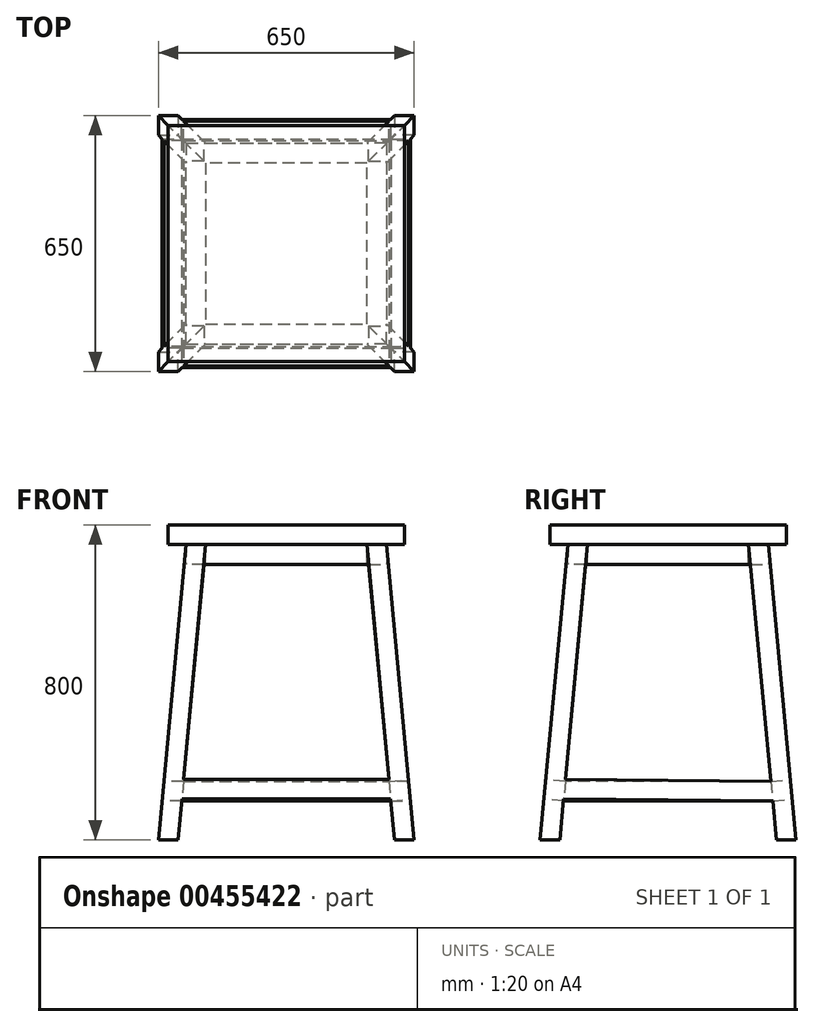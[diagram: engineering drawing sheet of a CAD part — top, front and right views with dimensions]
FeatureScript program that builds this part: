
annotation { "Feature Type Name" : "Feature", "Feature Type Description" : "" }
export const myFeature = defineFeature(function(context is Context, id is Id, definition is map)
    precondition{}
    {
        {
            var Q0;
            Q0=qCreatedBy(makeId("Top.planeOp"),FACE);
            var sketch = newSketch(context, id + "F0", { "sketchPlane" : qUnion([Q0])});
            skLineSegment(sketch, "E0.bottom", {"start": v(-250, 250) * mm, "end": v(250, 250) * mm, "construction": true});
            skLineSegment(sketch, "E0.top", {"start": v(-250, -250) * mm, "end": v(250, -250) * mm, "construction": true});
            skLineSegment(sketch, "E0.left", {"start": v(-250, 250) * mm, "end": v(-250, -250) * mm, "construction": true});
            skLineSegment(sketch, "E0.right", {"start": v(250, 250) * mm, "end": v(250, -250) * mm, "construction": true});
            skPoint(sketch, "E0.middle", {"position": v(0, 0) * mm});
            skLineSegment(sketch, "E1.bottom", {"start": v(-250, -250) * mm, "end": v(-200, -250) * mm});
            skLineSegment(sketch, "E1.top", {"start": v(-250, -200) * mm, "end": v(-200, -200) * mm});
            skLineSegment(sketch, "E1.left", {"start": v(-250, -250) * mm, "end": v(-250, -200) * mm});
            skLineSegment(sketch, "E1.right", {"start": v(-200, -250) * mm, "end": v(-200, -200) * mm});
            skLineSegment(sketch, "E2.bottom", {"start": v(250, -250) * mm, "end": v(200, -250) * mm});
            skLineSegment(sketch, "E2.top", {"start": v(250, -200) * mm, "end": v(200, -200) * mm});
            skLineSegment(sketch, "E2.left", {"start": v(250, -250) * mm, "end": v(250, -200) * mm});
            skLineSegment(sketch, "E2.right", {"start": v(200, -250) * mm, "end": v(200, -200) * mm});
            skLineSegment(sketch, "E3.bottom", {"start": v(250, 250) * mm, "end": v(200, 250) * mm});
            skLineSegment(sketch, "E3.top", {"start": v(250, 200) * mm, "end": v(200, 200) * mm});
            skLineSegment(sketch, "E3.left", {"start": v(250, 250) * mm, "end": v(250, 200) * mm});
            skLineSegment(sketch, "E3.right", {"start": v(200, 250) * mm, "end": v(200, 200) * mm});
            skLineSegment(sketch, "E4.bottom", {"start": v(-250, 250) * mm, "end": v(-200, 250) * mm});
            skLineSegment(sketch, "E4.top", {"start": v(-250, 200) * mm, "end": v(-200, 200) * mm});
            skLineSegment(sketch, "E4.left", {"start": v(-250, 250) * mm, "end": v(-250, 200) * mm});
            skLineSegment(sketch, "E4.right", {"start": v(-200, 250) * mm, "end": v(-200, 200) * mm});
            skSolve(sketch);
        }
        {
            var Q0;
            Q0=qCreatedBy(makeId("Top.planeOp"),FACE);
            cPlane(context, id + "F1", {"entities" : qUnion([Q0]), "cplaneType" : CPlaneType.OFFSET, "offset" : 800 * mm, "oppositeDirection" : true, "width" : 150 * mm, "height" : 150 * mm});
        }
        {
            var Q0;
            Q0=qCreatedBy(id+"F1.planeOp",FACE);
            var sketch = newSketch(context, id + "F2", { "sketchPlane" : qUnion([Q0])});
            skLineSegment(sketch, "E5.bottom", {"start": v(-325, 325) * mm, "end": v(325, 325) * mm, "construction": true});
            skLineSegment(sketch, "E5.top", {"start": v(-325, -325) * mm, "end": v(325, -325) * mm, "construction": true});
            skLineSegment(sketch, "E5.left", {"start": v(-325, 325) * mm, "end": v(-325, -325) * mm, "construction": true});
            skLineSegment(sketch, "E5.right", {"start": v(325, 325) * mm, "end": v(325, -325) * mm, "construction": true});
            skPoint(sketch, "E5.middle", {"position": v(0, 0) * mm});
            skLineSegment(sketch, "E6.bottom", {"start": v(-325, -325) * mm, "end": v(-275, -325) * mm});
            skLineSegment(sketch, "E6.top", {"start": v(-325, -275) * mm, "end": v(-275, -275) * mm});
            skLineSegment(sketch, "E6.left", {"start": v(-325, -325) * mm, "end": v(-325, -275) * mm});
            skLineSegment(sketch, "E6.right", {"start": v(-275, -325) * mm, "end": v(-275, -275) * mm});
            skLineSegment(sketch, "E7.bottom", {"start": v(325, -325) * mm, "end": v(275, -325) * mm});
            skLineSegment(sketch, "E7.top", {"start": v(325, -275) * mm, "end": v(275, -275) * mm});
            skLineSegment(sketch, "E7.left", {"start": v(325, -325) * mm, "end": v(325, -275) * mm});
            skLineSegment(sketch, "E7.right", {"start": v(275, -325) * mm, "end": v(275, -275) * mm});
            skLineSegment(sketch, "E8.bottom", {"start": v(325, 325) * mm, "end": v(275, 325) * mm});
            skLineSegment(sketch, "E8.top", {"start": v(325, 275) * mm, "end": v(275, 275) * mm});
            skLineSegment(sketch, "E8.left", {"start": v(325, 325) * mm, "end": v(325, 275) * mm});
            skLineSegment(sketch, "E8.right", {"start": v(275, 325) * mm, "end": v(275, 275) * mm});
            skLineSegment(sketch, "E9.bottom", {"start": v(-325, 325) * mm, "end": v(-275, 325) * mm});
            skLineSegment(sketch, "E9.top", {"start": v(-325, 275) * mm, "end": v(-275, 275) * mm});
            skLineSegment(sketch, "E9.left", {"start": v(-325, 325) * mm, "end": v(-325, 275) * mm});
            skLineSegment(sketch, "E9.right", {"start": v(-275, 325) * mm, "end": v(-275, 275) * mm});
            skSolve(sketch);
        }
        {
            var Q0;
            Q0=qCreatedBy(makeId("Top.planeOp"),FACE);
            var sketch = newSketch(context, id + "F3", { "sketchPlane" : qUnion([Q0])});
            skLineSegment(sketch, "E10.bottom", {"start": v(-300, 300) * mm, "end": v(300, 300) * mm});
            skLineSegment(sketch, "E10.top", {"start": v(-300, -300) * mm, "end": v(300, -300) * mm});
            skLineSegment(sketch, "E10.left", {"start": v(-300, 300) * mm, "end": v(-300, -300) * mm});
            skLineSegment(sketch, "E10.right", {"start": v(300, 300) * mm, "end": v(300, -300) * mm});
            skPoint(sketch, "E10.middle", {"position": v(0, 0) * mm});
            skSolve(sketch);
        }
        {
            var Q0;
            Q0=makeQuery(id+"F0.imprint","IMPRINT",FACE,{"disambiguationData":[TD([[makeQuery(id+"F0.imprint","IMPRINT",EDGE,{"derivedFrom":sQuery(id+"F0.wireOp",EDGE,"E1.bottom")}),1.0]])]});
            var Q1;
            Q1=makeQuery(id+"F2.imprint","IMPRINT",FACE,{"disambiguationData":[TD([[makeQuery(id+"F2.imprint","IMPRINT",EDGE,{"derivedFrom":sQuery(id+"F2.wireOp",EDGE,"E6.bottom")}),1.0]])]});
            loft(context, id + "F4", {"sheetProfilesArray" : [{ "sheetProfileEntities" : qUnion([Q0]) }, { "sheetProfileEntities" : qUnion([Q1]) }]});
        }
        {
            var Q0;
            Q0=makeQuery(id+"F0.imprint","IMPRINT",FACE,{"disambiguationData":[TD([[makeQuery(id+"F0.imprint","IMPRINT",EDGE,{"derivedFrom":sQuery(id+"F0.wireOp",EDGE,"E2.bottom")}),-1.0]])]});
            var Q1;
            Q1=makeQuery(id+"F2.imprint","IMPRINT",FACE,{"disambiguationData":[TD([[makeQuery(id+"F2.imprint","IMPRINT",EDGE,{"derivedFrom":sQuery(id+"F2.wireOp",EDGE,"E7.bottom")}),-1.0]])]});
            loft(context, id + "F5", {"sheetProfilesArray" : [{ "sheetProfileEntities" : qUnion([Q0]) }, { "sheetProfileEntities" : qUnion([Q1]) }]});
        }
        {
            var Q0;
            Q0=makeQuery(id+"F0.imprint","IMPRINT",FACE,{"disambiguationData":[TD([[makeQuery(id+"F0.imprint","IMPRINT",EDGE,{"derivedFrom":sQuery(id+"F0.wireOp",EDGE,"E4.bottom")}),-1.0]])]});
            var Q1;
            Q1=makeQuery(id+"F2.imprint","IMPRINT",FACE,{"disambiguationData":[TD([[makeQuery(id+"F2.imprint","IMPRINT",EDGE,{"derivedFrom":sQuery(id+"F2.wireOp",EDGE,"E9.bottom")}),-1.0]])]});
            loft(context, id + "F6", {"sheetProfilesArray" : [{ "sheetProfileEntities" : qUnion([Q0]) }, { "sheetProfileEntities" : qUnion([Q1]) }]});
        }
        {
            var Q0;
            Q0=makeQuery(id+"F0.imprint","IMPRINT",FACE,{"disambiguationData":[TD([[makeQuery(id+"F0.imprint","IMPRINT",EDGE,{"derivedFrom":sQuery(id+"F0.wireOp",EDGE,"E3.bottom")}),1.0]])]});
            var Q1;
            Q1=makeQuery(id+"F2.imprint","IMPRINT",FACE,{"disambiguationData":[TD([[makeQuery(id+"F2.imprint","IMPRINT",EDGE,{"derivedFrom":sQuery(id+"F2.wireOp",EDGE,"E8.bottom")}),1.0]])]});
            loft(context, id + "F7", {"sheetProfilesArray" : [{ "sheetProfileEntities" : qUnion([Q0]) }, { "sheetProfileEntities" : qUnion([Q1]) }]});
        }
        {
            var Q0;
            Q0 = qSketchRegion(id + "F3", true);
            extrude(context, id + "F8", {"entities" : qUnion([Q0]), "operationType" : NewBodyOperationType.ADD, "oppositeDirection" : true, "depth" : 50 * mm});
        }
        {
            var Q0;
            Q0=makeQuery(id+"F8.opExtrude","CAP_FACE",FACE,{"disambiguationData":[OSD([sQuery(id+"F3.wireOp",EDGE,"E10.bottom"),sQuery(id+"F3.wireOp",EDGE,"E10.top"),sQuery(id+"F3.wireOp",EDGE,"E10.left"),sQuery(id+"F3.wireOp",EDGE,"E10.right")])],"isStart":false});
            var sketch = newSketch(context, id + "F9", { "sketchPlane" : qUnion([Q0])});
            skLineSegment(sketch, "E11", {"start": v(204.69, 204.69) * mm, "end": v(204.69, -204.69) * mm});
            skLineSegment(sketch, "E12", {"start": v(254.69, -204.69) * mm, "end": v(254.69, 204.69) * mm});
            skLineSegment(sketch, "E13", {"start": v(-204.69, -204.69) * mm, "end": v(-204.69, 204.69) * mm});
            skLineSegment(sketch, "E14", {"start": v(-204.69, 204.69) * mm, "end": v(204.69, 204.69) * mm});
            skLineSegment(sketch, "E15", {"start": v(204.69, 254.69) * mm, "end": v(-204.69, 254.69) * mm});
            skLineSegment(sketch, "E16", {"start": v(204.69, -254.69) * mm, "end": v(-204.69, -254.69) * mm});
            skLineSegment(sketch, "E17", {"start": v(-204.69, 254.69) * mm, "end": v(-254.69, 254.69) * mm});
            skLineSegment(sketch, "E18", {"start": v(-254.69, 254.69) * mm, "end": v(-254.69, -254.69) * mm});
            skLineSegment(sketch, "E19", {"start": v(-254.69, -254.69) * mm, "end": v(-204.69, -254.69) * mm});
            skLineSegment(sketch, "E20", {"start": v(204.69, -254.69) * mm, "end": v(254.69, -254.69) * mm});
            skLineSegment(sketch, "E21", {"start": v(254.69, -254.69) * mm, "end": v(254.69, -204.69) * mm});
            skLineSegment(sketch, "E22", {"start": v(254.69, 204.69) * mm, "end": v(254.69, 254.69) * mm});
            skLineSegment(sketch, "E23", {"start": v(254.69, 254.69) * mm, "end": v(204.69, 254.69) * mm});
            skLineSegment(sketch, "E24", {"start": v(204.69, -204.69) * mm, "end": v(-204.69, -204.69) * mm});
            skSolve(sketch);
        }
        {
            var Q0;
            Q0 = qSketchRegion(id + "F9", true);
            extrude(context, id + "F10", {"entities" : qUnion([Q0]), "operationType" : NewBodyOperationType.ADD, "depth" : 50 * mm});
        }
        {
            var Q0;
            Q0=qCreatedBy(id+"F1.planeOp",FACE);
            cPlane(context, id + "F11", {"entities" : qUnion([Q0]), "cplaneType" : CPlaneType.OFFSET, "offset" : 80 * mm, "width" : 150 * mm, "height" : 150 * mm});
        }
        {
            var Q0;
            Q0=makeQuery(id+"F6.opLoft","SWEPT_FACE",FACE,{"disambiguationData":[OSD([sQuery(id+"F0.wireOp",EDGE,"E4.top"),sQuery(id+"F0.wireOp",EDGE,"E4.left"),sQuery(id+"F0.wireOp",EDGE,"E4.right"),sQuery(id+"F2.wireOp",EDGE,"E9.top"),sQuery(id+"F2.wireOp",EDGE,"E9.left"),sQuery(id+"F2.wireOp",EDGE,"E9.right")])]});
            var sketch = newSketch(context, id + "F12", { "sketchPlane" : qUnion([Q0])});
            skLineSegment(sketch, "E25", {"start": v(-275, -822.18) * mm, "end": v(-265.7, -722.6) * mm, "construction": true});
            skLineSegment(sketch, "E26", {"start": v(-265.7, -722.6) * mm, "end": v(-261.06, -672.83) * mm});
            skLineSegment(sketch, "E27", {"start": v(-311.06, -672.83) * mm, "end": v(-315.7, -722.6) * mm});
            skLineSegment(sketch, "E28", {"start": v(-315.7, -722.6) * mm, "end": v(-265.7, -722.6) * mm});
            skLineSegment(sketch, "E29", {"start": v(-261.06, -672.83) * mm, "end": v(-311.06, -672.83) * mm});
            skSolve(sketch);
        }
        {
            var Q0;
            Q0=makeQuery(id+"F6.opLoft","SWEPT_FACE",FACE,{"disambiguationData":[OSD([sQuery(id+"F0.wireOp",EDGE,"E4.bottom"),sQuery(id+"F0.wireOp",EDGE,"E4.top"),sQuery(id+"F0.wireOp",EDGE,"E4.right"),sQuery(id+"F2.wireOp",EDGE,"E9.bottom"),sQuery(id+"F2.wireOp",EDGE,"E9.top"),sQuery(id+"F2.wireOp",EDGE,"E9.right")])]});
            var sketch = newSketch(context, id + "F13", { "sketchPlane" : qUnion([Q0])});
            skLineSegment(sketch, "E30", {"start": v(275, -822.18) * mm, "end": v(265.7, -722.6) * mm, "construction": true});
            skLineSegment(sketch, "E31", {"start": v(265.7, -722.6) * mm, "end": v(261.06, -672.83) * mm});
            skLineSegment(sketch, "E32", {"start": v(265.7, -722.6) * mm, "end": v(315.27, -717.98) * mm});
            skLineSegment(sketch, "E33", {"start": v(261.06, -672.83) * mm, "end": v(310.63, -668.2) * mm});
            skLineSegment(sketch, "E34", {"start": v(310.63, -668.2) * mm, "end": v(315.27, -717.98) * mm});
            skSolve(sketch);
        }
        {
            var Q0;
            Q0=makeQuery(id+"F7.opLoft","SWEPT_FACE",FACE,{"disambiguationData":[OSD([sQuery(id+"F0.wireOp",EDGE,"E3.bottom"),sQuery(id+"F0.wireOp",EDGE,"E3.top"),sQuery(id+"F0.wireOp",EDGE,"E3.right"),sQuery(id+"F2.wireOp",EDGE,"E8.bottom"),sQuery(id+"F2.wireOp",EDGE,"E8.top"),sQuery(id+"F2.wireOp",EDGE,"E8.right")])]});
            var sketch = newSketch(context, id + "F14", { "sketchPlane" : qUnion([Q0])});
            skLineSegment(sketch, "E35", {"start": v(-275, -822.18) * mm, "end": v(-265.7, -722.6) * mm, "construction": true});
            skLineSegment(sketch, "E36", {"start": v(-265.7, -722.6) * mm, "end": v(-261.06, -672.83) * mm});
            skLineSegment(sketch, "E37", {"start": v(-261.06, -672.83) * mm, "end": v(-310.63, -668.2) * mm});
            skLineSegment(sketch, "E38", {"start": v(-265.7, -722.6) * mm, "end": v(-315.27, -717.98) * mm});
            skLineSegment(sketch, "E39", {"start": v(-315.27, -717.98) * mm, "end": v(-310.63, -668.2) * mm});
            skSolve(sketch);
        }
        {
            var Q1;
            Q1=makeQuery(id+"F13.imprint","IMPRINT",FACE,{"disambiguationData":[TD([[makeQuery(id+"F13.imprint","IMPRINT",EDGE,{"derivedFrom":sQuery(id+"F13.wireOp",EDGE,"E31")}),1.0]])]});
            var Q2;
            Q2=makeQuery(id+"F14.imprint","IMPRINT",FACE,{"disambiguationData":[TD([[makeQuery(id+"F14.imprint","IMPRINT",EDGE,{"derivedFrom":sQuery(id+"F14.wireOp",EDGE,"E36")}),-1.0]])]});
            loft(context, id + "F15", {"operationType" : NewBodyOperationType.ADD, "sheetProfilesArray" : [{ "sheetProfileEntities" : qUnion([Q1]) }, { "sheetProfileEntities" : qUnion([Q2]) }]});
        }
        {
            var Q0;
            Q0=makeQuery(id+"F4.opLoft","SWEPT_FACE",FACE,{"disambiguationData":[OSD([sQuery(id+"F0.wireOp",EDGE,"E1.top"),sQuery(id+"F0.wireOp",EDGE,"E1.left"),sQuery(id+"F0.wireOp",EDGE,"E1.right"),sQuery(id+"F2.wireOp",EDGE,"E6.top"),sQuery(id+"F2.wireOp",EDGE,"E6.left"),sQuery(id+"F2.wireOp",EDGE,"E6.right")])]});
            var sketch = newSketch(context, id + "F16", { "sketchPlane" : qUnion([Q0])});
            skLineSegment(sketch, "E40", {"start": v(275, -822.18) * mm, "end": v(265.7, -722.6) * mm, "construction": true});
            skLineSegment(sketch, "E41", {"start": v(265.7, -722.6) * mm, "end": v(315.7, -722.6) * mm});
            skLineSegment(sketch, "E42", {"start": v(265.7, -722.6) * mm, "end": v(261.06, -672.83) * mm});
            skLineSegment(sketch, "E43", {"start": v(261.06, -672.83) * mm, "end": v(311.06, -672.83) * mm});
            skLineSegment(sketch, "E44", {"start": v(311.06, -672.83) * mm, "end": v(315.7, -722.6) * mm});
            skSolve(sketch);
        }
        {
            var Q0;
            Q0=makeQuery(id+"F4.opLoft","SWEPT_FACE",FACE,{"disambiguationData":[OSD([sQuery(id+"F0.wireOp",EDGE,"E1.bottom"),sQuery(id+"F0.wireOp",EDGE,"E1.top"),sQuery(id+"F0.wireOp",EDGE,"E1.right"),sQuery(id+"F2.wireOp",EDGE,"E6.bottom"),sQuery(id+"F2.wireOp",EDGE,"E6.top"),sQuery(id+"F2.wireOp",EDGE,"E6.right")])]});
            var sketch = newSketch(context, id + "F17", { "sketchPlane" : qUnion([Q0])});
            skLineSegment(sketch, "E45", {"start": v(-275, -822.18) * mm, "end": v(-265.7, -722.6) * mm, "construction": true});
            skLineSegment(sketch, "E46", {"start": v(-265.7, -722.6) * mm, "end": v(-261.06, -672.83) * mm});
            skLineSegment(sketch, "E47", {"start": v(-265.7, -722.6) * mm, "end": v(-315.27, -717.98) * mm});
            skLineSegment(sketch, "E48", {"start": v(-261.06, -672.83) * mm, "end": v(-310.63, -668.2) * mm});
            skLineSegment(sketch, "E49", {"start": v(-310.63, -668.2) * mm, "end": v(-315.27, -717.98) * mm});
            skSolve(sketch);
        }
        {
            var Q1;
            Q1=makeQuery(id+"F12.imprint","IMPRINT",FACE,{"disambiguationData":[TD([[makeQuery(id+"F12.imprint","IMPRINT",EDGE,{"derivedFrom":sQuery(id+"F12.wireOp",EDGE,"E26")}),-1.0]])]});
            var Q2;
            Q2=makeQuery(id+"F16.imprint","IMPRINT",FACE,{"disambiguationData":[TD([[makeQuery(id+"F16.imprint","IMPRINT",EDGE,{"derivedFrom":sQuery(id+"F16.wireOp",EDGE,"E41")}),1.0]])]});
            loft(context, id + "F18", {"operationType" : NewBodyOperationType.ADD, "sheetProfilesArray" : [{ "sheetProfileEntities" : qUnion([Q1]) }, { "sheetProfileEntities" : qUnion([Q2]) }]});
        }
        {
            var Q0;
            Q0=makeQuery(id+"F5.opLoft","SWEPT_FACE",FACE,{"disambiguationData":[OSD([sQuery(id+"F0.wireOp",EDGE,"E2.bottom"),sQuery(id+"F0.wireOp",EDGE,"E2.top"),sQuery(id+"F0.wireOp",EDGE,"E2.right"),sQuery(id+"F2.wireOp",EDGE,"E7.bottom"),sQuery(id+"F2.wireOp",EDGE,"E7.top"),sQuery(id+"F2.wireOp",EDGE,"E7.right")])]});
            var sketch = newSketch(context, id + "F19", { "sketchPlane" : qUnion([Q0])});
            skLineSegment(sketch, "E50", {"start": v(275, -822.18) * mm, "end": v(265.7, -722.6) * mm, "construction": true});
            skLineSegment(sketch, "E51", {"start": v(265.7, -722.6) * mm, "end": v(261.06, -672.83) * mm});
            skLineSegment(sketch, "E52", {"start": v(265.7, -722.6) * mm, "end": v(315.27, -717.98) * mm});
            skLineSegment(sketch, "E53", {"start": v(261.06, -672.83) * mm, "end": v(310.63, -668.2) * mm});
            skLineSegment(sketch, "E54", {"start": v(310.63, -668.2) * mm, "end": v(315.27, -717.98) * mm});
            skSolve(sketch);
        }
        {
            var Q0;
            Q0=makeQuery(id+"F5.opLoft","SWEPT_FACE",FACE,{"disambiguationData":[OSD([sQuery(id+"F0.wireOp",EDGE,"E2.top"),sQuery(id+"F0.wireOp",EDGE,"E2.left"),sQuery(id+"F0.wireOp",EDGE,"E2.right"),sQuery(id+"F2.wireOp",EDGE,"E7.top"),sQuery(id+"F2.wireOp",EDGE,"E7.left"),sQuery(id+"F2.wireOp",EDGE,"E7.right")])]});
            var sketch = newSketch(context, id + "F20", { "sketchPlane" : qUnion([Q0])});
            skLineSegment(sketch, "E55", {"start": v(-275, -822.18) * mm, "end": v(-265.7, -722.6) * mm, "construction": true});
            skLineSegment(sketch, "E56", {"start": v(-265.7, -722.6) * mm, "end": v(-261.06, -672.83) * mm});
            skLineSegment(sketch, "E57", {"start": v(-265.7, -722.6) * mm, "end": v(-315.27, -717.98) * mm});
            skLineSegment(sketch, "E58", {"start": v(-261.06, -672.83) * mm, "end": v(-310.63, -668.2) * mm});
            skLineSegment(sketch, "E59", {"start": v(-310.63, -668.2) * mm, "end": v(-315.27, -717.98) * mm});
            skSolve(sketch);
        }
        {
            var Q1;
            Q1=makeQuery(id+"F17.imprint","IMPRINT",FACE,{"disambiguationData":[TD([[makeQuery(id+"F17.imprint","IMPRINT",EDGE,{"derivedFrom":sQuery(id+"F17.wireOp",EDGE,"E46")}),-1.0]])]});
            var Q2;
            Q2=makeQuery(id+"F19.imprint","IMPRINT",FACE,{"disambiguationData":[TD([[makeQuery(id+"F19.imprint","IMPRINT",EDGE,{"derivedFrom":sQuery(id+"F19.wireOp",EDGE,"E51")}),1.0]])]});
            loft(context, id + "F21", {"operationType" : NewBodyOperationType.ADD, "sheetProfilesArray" : [{ "sheetProfileEntities" : qUnion([Q1]) }, { "sheetProfileEntities" : qUnion([Q2]) }]});
        }
        {
            var Q0;
            {var subQ0=sQuery(id+"F9.wireOp",EDGE,"E22");var subQ1=sQuery(id+"F9.wireOp",EDGE,"E21");var subQ2=sQuery(id+"F9.wireOp",EDGE,"E12");var subQ3=sQuery(id+"F2.wireOp",EDGE,"E8.left");var subQ4=sQuery(id+"F2.wireOp",EDGE,"E8.top");var subQ6=sQuery(id+"F0.wireOp",EDGE,"E3.left");var subQ7=sQuery(id+"F0.wireOp",EDGE,"E3.top");var subQ9=sQuery(id+"F2.wireOp",EDGE,"E8.right");var subQ16=sQuery(id+"F2.wireOp",EDGE,"E9.right");var subQ17=sQuery(id+"F2.wireOp",EDGE,"E9.top");var subQ20=sQuery(id+"F0.wireOp",EDGE,"E4.right");var subQ21=sQuery(id+"F0.wireOp",EDGE,"E4.top");var subQ24=sQuery(id+"F0.wireOp",EDGE,"E3.right");var subQ25=makeQuery(id+"F7.opLoft","SWEPT_FACE",FACE,{"disambiguationData":[OSD([subQ7,subQ6,subQ24,subQ4,subQ3,subQ9])]});var subQ29=sQuery(id+"F14.wireOp",EDGE,"E37");var subQ30=sQuery(id+"F14.wireOp",EDGE,"E36");var subQ32=sQuery(id+"F13.wireOp",EDGE,"E33");var subQ33=sQuery(id+"F13.wireOp",EDGE,"E31");var subQ34=sQuery(id+"F2.wireOp",EDGE,"E9.left");var subQ35=sQuery(id+"F0.wireOp",EDGE,"E4.left");var subQ36=makeQuery(id+"F6.opLoft","SWEPT_FACE",FACE,{"disambiguationData":[OSD([subQ21,subQ35,subQ20,subQ17,subQ34,subQ16])]});var subQ37=sQuery(id+"F14.wireOp",EDGE,"E38");var subQ38=sQuery(id+"F13.wireOp",EDGE,"E32");var subQ39=makeQuery(id+"F15.opLoft","SWEPT_FACE",FACE,{"disambiguationData":[OSD([subQ7,subQ24,subQ21,subQ20,subQ4,subQ9,subQ17,subQ16,subQ33,subQ38,subQ32,subQ30,subQ29,subQ37])]});Q0=makeQuery(id+"F18.boolean.opBoolean","SPLIT",FACE,{"disambiguationData":[TD([makeQuery(id+"F10.opExtrude","SWEPT_FACE",FACE,{"disambiguationData":[OSD([subQ2,subQ1,subQ0])]})])],"derivedFrom":makeQuery(id+"F15.boolean.opBoolean","MERGE",FACE,{"derivedFrom":[subQ36,subQ25,subQ39]})});}
            var sketch = newSketch(context, id + "F22", { "sketchPlane" : qUnion([Q0])});
            skLineSegment(sketch, "E60", {"start": v(275, -822.18) * mm, "end": v(265.7, -722.6) * mm, "construction": true});
            skLineSegment(sketch, "E61", {"start": v(265.7, -722.6) * mm, "end": v(315.7, -722.6) * mm});
            skLineSegment(sketch, "E62", {"start": v(315.7, -722.6) * mm, "end": v(311.06, -672.83) * mm});
            skLineSegment(sketch, "E63", {"start": v(311.06, -672.83) * mm, "end": v(261.06, -672.83) * mm});
            skLineSegment(sketch, "E64", {"start": v(261.06, -672.83) * mm, "end": v(265.7, -722.6) * mm});
            skSolve(sketch);
        }
        {
            var Q1;
            Q1=makeQuery(id+"F22.imprint","IMPRINT",FACE,{"disambiguationData":[TD([[makeQuery(id+"F22.imprint","IMPRINT",EDGE,{"derivedFrom":sQuery(id+"F22.wireOp",EDGE,"E61")}),1.0]])]});
            var Q2;
            Q2=makeQuery(id+"F20.imprint","IMPRINT",FACE,{"disambiguationData":[TD([[makeQuery(id+"F20.imprint","IMPRINT",EDGE,{"derivedFrom":sQuery(id+"F20.wireOp",EDGE,"E56")}),-1.0]])]});
            loft(context, id + "F23", {"operationType" : NewBodyOperationType.ADD, "sheetProfilesArray" : [{ "sheetProfileEntities" : qUnion([Q1]) }, { "sheetProfileEntities" : qUnion([Q2]) }]});
        }
    });
